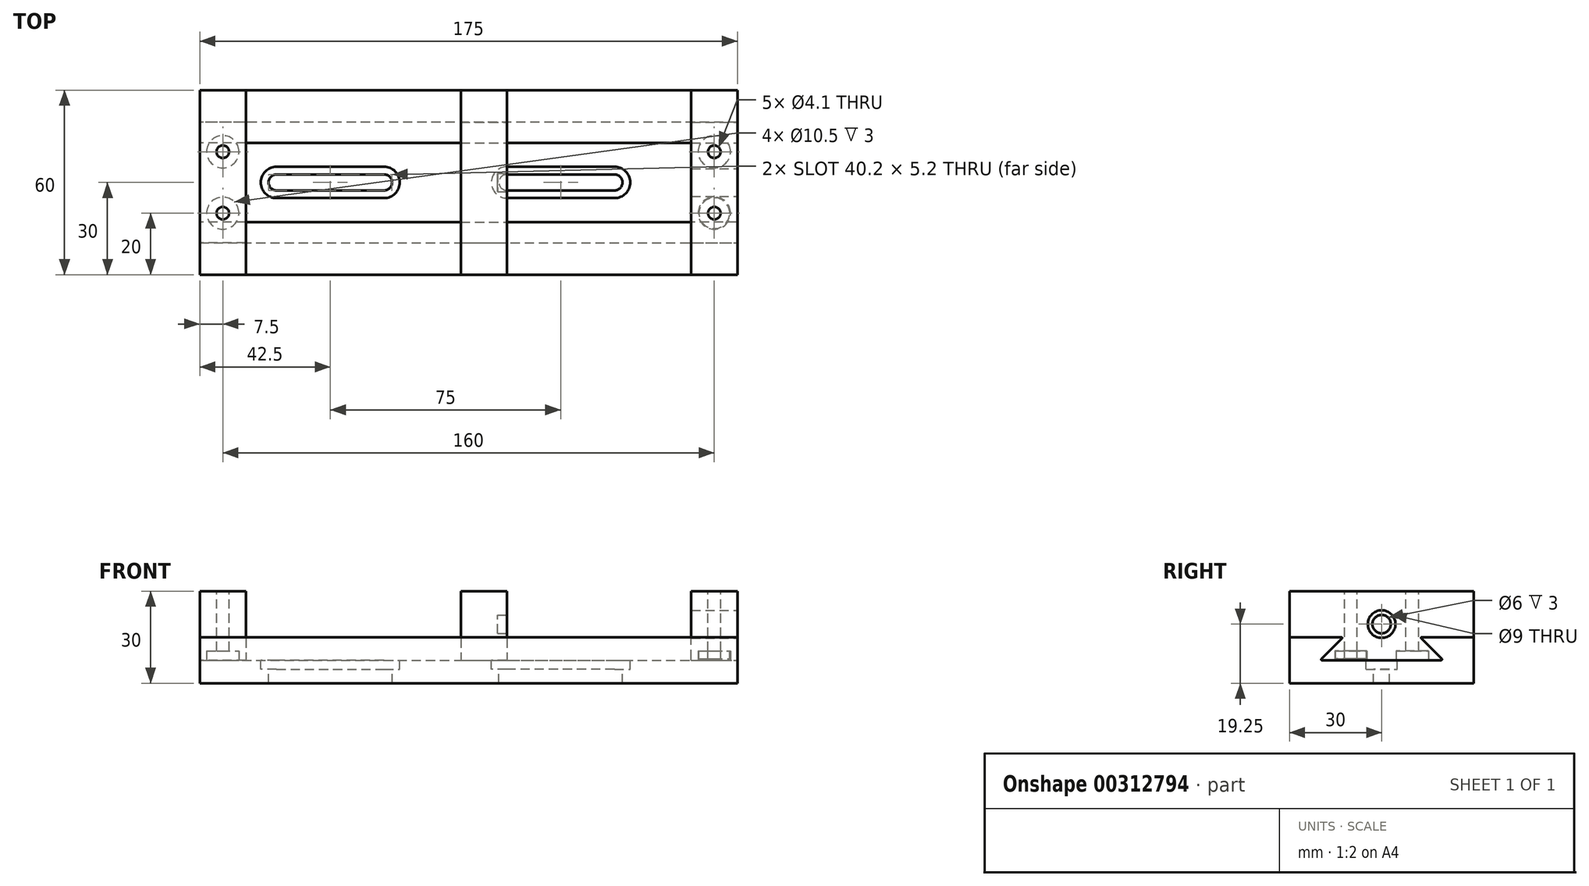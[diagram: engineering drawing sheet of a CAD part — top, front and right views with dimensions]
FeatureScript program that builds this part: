
annotation { "Feature Type Name" : "Feature", "Feature Type Description" : "" }
export const myFeature = defineFeature(function(context is Context, id is Id, definition is map)
    precondition{}
    {
        {
            var Q0;
            Q0=qCreatedBy(makeId("Top.planeOp"),FACE);
            var sketch = newSketch(context, id + "F0", { "sketchPlane" : qUnion([Q0])});
            skLineSegment(sketch, "E0.bottom", {"start": v(87.5, -30) * mm, "end": v(-87.5, -30) * mm});
            skLineSegment(sketch, "E0.top", {"start": v(87.5, 30) * mm, "end": v(-87.5, 30) * mm});
            skLineSegment(sketch, "E0.left", {"start": v(87.5, -30) * mm, "end": v(87.5, 30) * mm});
            skLineSegment(sketch, "E0.right", {"start": v(-87.5, -30) * mm, "end": v(-87.5, 30) * mm});
            skPoint(sketch, "E0.middle", {"position": v(0, 0) * mm});
            skSolve(sketch);
        }
        {
            var Q0;
            Q0=makeQuery(id+"F0.imprint","IMPRINT",FACE,{"disambiguationData":[TD([[makeQuery(id+"F0.imprint","IMPRINT",EDGE,{"derivedFrom":sQuery(id+"F0.wireOp",EDGE,"E0.bottom")}),-1.0]])]});
            extrude(context, id + "F1", {"entities" : qUnion([Q0]), "depth" : 15 * mm});
        }
        {
            var Q0;
            Q0=makeQuery(id+"F1.opExtrude","SWEPT_FACE",FACE,{"disambiguationData":[OSD([sQuery(id+"F0.wireOp",EDGE,"E0.left")])]});
            var sketch = newSketch(context, id + "F2", { "sketchPlane" : qUnion([Q0])});
            skLineSegment(sketch, "E1", {"start": v(-30, 7.5) * mm, "end": v(30, 7.5) * mm});
            skLineSegment(sketch, "E2", {"start": v(-20, 7.5) * mm, "end": v(-8.89, 18.61) * mm});
            skLineSegment(sketch, "E3", {"start": v(20, 7.5) * mm, "end": v(9.76, 17.74) * mm});
            skLineSegment(sketch, "E4", {"start": v(-8.89, 18.61) * mm, "end": v(9.76, 17.74) * mm});
            skSolve(sketch);
        }
        {
            var Q0;
            {var subQ0=sQuery(id+"F2.wireOp",EDGE,"E2");var subQ1=sQuery(id+"F2.wireOp",EDGE,"E1");var subQ2=makeQuery(id+"F2.imprint","INTERSECT",VERTEX,{"derivedFrom":[subQ1,subQ0]});Q0=makeQuery(id+"F2.imprint","IMPRINT",FACE,{"disambiguationData":[TD([[makeQuery(id+"F2.imprint","IMPRINT",EDGE,{"disambiguationData":[TD([[subQ2,-1.0]])],"derivedFrom":subQ1}),1.0]])]});}
            var Q1;
            {var subQ0=sQuery(id+"F2.wireOp",EDGE,"E4");Q1=makeQuery(id+"F2.imprint","IMPRINT",FACE,{"disambiguationData":[TD([[makeQuery(id+"F2.imprint","IMPRINT",EDGE,{"derivedFrom":subQ0}),-1.0]])]});}
            extrude(context, id + "F3", {"entities" : qUnion([Q0, Q1]), "operationType" : NewBodyOperationType.REMOVE, "endBound" : BoundingType.THROUGH_ALL, "oppositeDirection" : true, "depth" : 25 * mm});
        }
        {
            var Q0;
            Q0=makeQuery(id+"F3.boolean.opBoolean","COPY",EDGE,{"derivedFrom":makeQuery(id+"F3.opExtrude","SWEPT_EDGE",EDGE,{"disambiguationData":[OSD([sQuery(id+"F2.wireOp",EDGE,"E1"),sQuery(id+"F2.wireOp",EDGE,"E2")])]})});
            var Q1;
            Q1=makeQuery(id+"F3.boolean.opBoolean","COPY",EDGE,{"derivedFrom":makeQuery(id+"F3.opExtrude","SWEPT_EDGE",EDGE,{"disambiguationData":[OSD([sQuery(id+"F2.wireOp",EDGE,"E1"),sQuery(id+"F2.wireOp",EDGE,"E3")])]})});
            var Q2;
            Q2=makeQuery(id+"F3.boolean.opBoolean","INTERSECT",EDGE,{"derivedFrom":[makeQuery(id+"F1.opExtrude","CAP_FACE",FACE,{"disambiguationData":[OSD([sQuery(id+"F0.wireOp",EDGE,"E0.bottom"),sQuery(id+"F0.wireOp",EDGE,"E0.top"),sQuery(id+"F0.wireOp",EDGE,"E0.left"),sQuery(id+"F0.wireOp",EDGE,"E0.right")])],"isStart":false}),makeQuery(id+"F3.opExtrude","SWEPT_FACE",FACE,{"disambiguationData":[OSD([sQuery(id+"F2.wireOp",EDGE,"E3")])]})]});
            var Q3;
            Q3=makeQuery(id+"F3.boolean.opBoolean","INTERSECT",EDGE,{"derivedFrom":[makeQuery(id+"F1.opExtrude","CAP_FACE",FACE,{"disambiguationData":[OSD([sQuery(id+"F0.wireOp",EDGE,"E0.bottom"),sQuery(id+"F0.wireOp",EDGE,"E0.top"),sQuery(id+"F0.wireOp",EDGE,"E0.left"),sQuery(id+"F0.wireOp",EDGE,"E0.right")])],"isStart":false}),makeQuery(id+"F3.opExtrude","SWEPT_FACE",FACE,{"disambiguationData":[OSD([sQuery(id+"F2.wireOp",EDGE,"E2")])]})]});
            fillet(context, id + "F4", {"entities" : qUnion([Q0, Q1, Q2, Q3]), "radius" : .25 * mm, "tangentPropagation" : true, "allowEdgeOverflow" : false});
        }
        {
            var Q0;
            Q0=makeQuery(id+"F1.opExtrude","SWEPT_FACE",FACE,{"disambiguationData":[OSD([sQuery(id+"F0.wireOp",EDGE,"E0.left")])]});
            var sketch = newSketch(context, id + "F5", { "sketchPlane" : qUnion([Q0])});
            skLineSegment(sketch, "E5.0.0", {"start": v(30, 15) * mm, "end": v(13.1, 15) * mm});
            skArc(sketch, "E5.0.1", {"start": v(13.1, 15) * mm, "mid": v(12.87, 14.85) * mm, "end": v(12.93, 14.57) * mm});
            skLineSegment(sketch, "E5.0.2", {"start": v(12.93, 14.57) * mm, "end": v(19.57, 7.93) * mm});
            skArc(sketch, "E5.0.3", {"start": v(19.57, 7.93) * mm, "mid": v(19.63, 7.65) * mm, "end": v(19.4, 7.5) * mm});
            skLineSegment(sketch, "E5.0.4", {"start": v(19.4, 7.5) * mm, "end": v(-19.4, 7.5) * mm});
            skArc(sketch, "E5.0.5", {"start": v(-19.4, 7.5) * mm, "mid": v(-19.63, 7.65) * mm, "end": v(-19.57, 7.93) * mm});
            skLineSegment(sketch, "E5.0.6", {"start": v(-19.57, 7.93) * mm, "end": v(-12.93, 14.57) * mm});
            skArc(sketch, "E5.0.7", {"start": v(-12.93, 14.57) * mm, "mid": v(-12.87, 14.85) * mm, "end": v(-13.1, 15) * mm});
            skLineSegment(sketch, "E5.0.8", {"start": v(-13.1, 15) * mm, "end": v(-30, 15) * mm});
            skLineSegment(sketch, "E6.bottom", {"start": v(-30, 15) * mm, "end": v(-13.1, 15) * mm});
            skLineSegment(sketch, "E6.top", {"start": v(-30, 30) * mm, "end": v(30, 30) * mm});
            skLineSegment(sketch, "E6.left", {"start": v(-30, 15) * mm, "end": v(-30, 30) * mm});
            skLineSegment(sketch, "E6.right", {"start": v(30, 15) * mm, "end": v(30, 30) * mm});
            skLineSegment(sketch, "E7.trimOffspring", {"start": v(13.1, 15) * mm, "end": v(30, 15) * mm});
            skPoint(sketch, "E5.0.10.end.orphan", {"position": v(30, 0) * mm});
            skPoint(sketch, "E5.0.9.end.orphan", {"position": v(-30, 0) * mm});
            skSolve(sketch);
        }
        {
            var Q0;
            Q0=makeQuery(id+"F5.imprint","IMPRINT",FACE,{"disambiguationData":[TD([[makeQuery(id+"F5.imprint","IMPRINT",EDGE,{"derivedFrom":sQuery(id+"F5.wireOp",EDGE,"E5.0.1")}),-1.0]])]});
            extrude(context, id + "F6", {"entities" : qUnion([Q0]), "oppositeDirection" : true, "depth" : 15 * mm});
        }
        {
            var Q0;
            Q0=makeQuery(id+"F6.opExtrude","CAP_FACE",FACE,{"disambiguationData":[OSD([sQuery(id+"F5.wireOp",EDGE,"E5.0.1"),sQuery(id+"F5.wireOp",EDGE,"E5.0.2"),sQuery(id+"F5.wireOp",EDGE,"E5.0.3"),sQuery(id+"F5.wireOp",EDGE,"E5.0.4"),sQuery(id+"F5.wireOp",EDGE,"E5.0.5"),sQuery(id+"F5.wireOp",EDGE,"E5.0.6"),sQuery(id+"F5.wireOp",EDGE,"E5.0.7"),sQuery(id+"F5.wireOp",EDGE,"E6.bottom"),sQuery(id+"F5.wireOp",EDGE,"E6.top"),sQuery(id+"F5.wireOp",EDGE,"E6.left"),sQuery(id+"F5.wireOp",EDGE,"E6.right"),sQuery(id+"F5.wireOp",EDGE,"E7.trimOffspring")])],"isStart":true});
            var sketch = newSketch(context, id + "F7", { "sketchPlane" : qUnion([Q0])});
            skCircle(sketch, "E8", {"center": v(0, 19.25) * mm, "radius": 4.5 * mm});
            skLineSegment(sketch, "E9", {"start": v(0, 7.5) * mm, "end": v(0, 30) * mm, "construction": true});
            skSolve(sketch);
        }
        {
            var Q0;
            Q0=makeQuery(id+"F7.imprint","IMPRINT",FACE,{"disambiguationData":[TD([[makeQuery(id+"F7.imprint","IMPRINT",EDGE,{"derivedFrom":sQuery(id+"F7.wireOp",EDGE,"E8")}),1.0]])]});
            extrude(context, id + "F8", {"entities" : qUnion([Q0]), "operationType" : NewBodyOperationType.REMOVE, "endBound" : BoundingType.THROUGH_ALL, "oppositeDirection" : true, "depth" : 25 * mm});
        }
        {
            var Q0;
            Q0=makeQuery(id+"F1.opExtrude","SWEPT_FACE",FACE,{"disambiguationData":[OSD([sQuery(id+"F0.wireOp",EDGE,"E0.right")])]});
            var sketch = newSketch(context, id + "F9", { "sketchPlane" : qUnion([Q0])});
            skLineSegment(sketch, "E10.0.0", {"start": v(-19.57, 7.93) * mm, "end": v(-12.93, 14.57) * mm});
            skArc(sketch, "E10.0.1", {"start": v(-12.93, 14.57) * mm, "mid": v(-12.87, 14.85) * mm, "end": v(-13.1, 15) * mm});
            skLineSegment(sketch, "E10.0.2", {"start": v(-13.1, 15) * mm, "end": v(-30, 15) * mm});
            skLineSegment(sketch, "E10.0.6", {"start": v(30, 15) * mm, "end": v(13.1, 15) * mm});
            skArc(sketch, "E10.0.7", {"start": v(13.1, 15) * mm, "mid": v(12.87, 14.85) * mm, "end": v(12.93, 14.57) * mm});
            skLineSegment(sketch, "E10.0.8", {"start": v(12.93, 14.57) * mm, "end": v(19.57, 7.93) * mm});
            skArc(sketch, "E10.0.9", {"start": v(19.57, 7.93) * mm, "mid": v(19.63, 7.65) * mm, "end": v(19.4, 7.5) * mm});
            skLineSegment(sketch, "E10.0.10", {"start": v(19.4, 7.5) * mm, "end": v(-19.4, 7.5) * mm});
            skArc(sketch, "E10.0.11", {"start": v(-19.4, 7.5) * mm, "mid": v(-19.63, 7.65) * mm, "end": v(-19.57, 7.93) * mm});
            skLineSegment(sketch, "E11.bottom", {"start": v(-30, 15) * mm, "end": v(-13.1, 15) * mm});
            skLineSegment(sketch, "E11.top", {"start": v(-30, 30) * mm, "end": v(30, 30) * mm});
            skLineSegment(sketch, "E11.left", {"start": v(-30, 15) * mm, "end": v(-30, 30) * mm});
            skLineSegment(sketch, "E11.right", {"start": v(30, 15) * mm, "end": v(30, 30) * mm});
            skLineSegment(sketch, "E12.trimOffspring", {"start": v(13.1, 15) * mm, "end": v(30, 15) * mm});
            skPoint(sketch, "E10.0.4.end.orphan", {"position": v(30, 0) * mm});
            skPoint(sketch, "E10.0.3.end.orphan", {"position": v(-30, 0) * mm});
            skSolve(sketch);
        }
        {
            var Q0;
            Q0=makeQuery(id+"F9.imprint","IMPRINT",FACE,{"disambiguationData":[TD([[makeQuery(id+"F9.imprint","IMPRINT",EDGE,{"derivedFrom":sQuery(id+"F9.wireOp",EDGE,"E10.0.0")}),1.0]])]});
            extrude(context, id + "F10", {"entities" : qUnion([Q0]), "oppositeDirection" : true, "depth" : 15 * mm});
        }
        {
            var Q0;
            Q0=makeQuery(id+"F1.opExtrude","SWEPT_FACE",FACE,{"disambiguationData":[OSD([sQuery(id+"F0.wireOp",EDGE,"E0.right")])]});
            cPlane(context, id + "F11", {"entities" : qUnion([Q0]), "cplaneType" : CPlaneType.OFFSET, "offset" : 100 * mm, "oppositeDirection" : true, "width" : 150 * mm, "height" : 150 * mm});
        }
        {
            var Q0;
            Q0=qCreatedBy(id+"F11.planeOp",FACE);
            var sketch = newSketch(context, id + "F12", { "sketchPlane" : qUnion([Q0])});
            skLineSegment(sketch, "E13.0.0", {"start": v(-19.57, 7.93) * mm, "end": v(-12.93, 14.57) * mm});
            skArc(sketch, "E13.0.1", {"start": v(-12.93, 14.57) * mm, "mid": v(-12.87, 14.85) * mm, "end": v(-13.1, 15) * mm});
            skLineSegment(sketch, "E13.0.2", {"start": v(-13.1, 15) * mm, "end": v(-30, 15) * mm});
            skLineSegment(sketch, "E13.0.6", {"start": v(30, 15) * mm, "end": v(13.1, 15) * mm});
            skArc(sketch, "E13.0.7", {"start": v(13.1, 15) * mm, "mid": v(12.87, 14.85) * mm, "end": v(12.93, 14.57) * mm});
            skLineSegment(sketch, "E13.0.8", {"start": v(12.93, 14.57) * mm, "end": v(19.57, 7.93) * mm});
            skArc(sketch, "E13.0.9", {"start": v(19.57, 7.93) * mm, "mid": v(19.63, 7.65) * mm, "end": v(19.4, 7.5) * mm});
            skLineSegment(sketch, "E13.0.10", {"start": v(19.4, 7.5) * mm, "end": v(-19.4, 7.5) * mm});
            skArc(sketch, "E13.0.11", {"start": v(-19.4, 7.5) * mm, "mid": v(-19.63, 7.65) * mm, "end": v(-19.57, 7.93) * mm});
            skLineSegment(sketch, "E14.bottom", {"start": v(-30, 15) * mm, "end": v(-13.1, 15) * mm});
            skLineSegment(sketch, "E14.top", {"start": v(-30, 30) * mm, "end": v(30, 30) * mm});
            skLineSegment(sketch, "E14.left", {"start": v(-30, 15) * mm, "end": v(-30, 30) * mm});
            skLineSegment(sketch, "E14.right", {"start": v(30, 15) * mm, "end": v(30, 30) * mm});
            skLineSegment(sketch, "E15.trimOffspring", {"start": v(13.1, 15) * mm, "end": v(30, 15) * mm});
            skPoint(sketch, "E13.0.4.end.orphan", {"position": v(30, 0) * mm});
            skPoint(sketch, "E13.0.3.end.orphan", {"position": v(-30, 0) * mm});
            skSolve(sketch);
        }
        {
            var Q0;
            Q0=makeQuery(id+"F12.imprint","IMPRINT",FACE,{"disambiguationData":[TD([[makeQuery(id+"F12.imprint","IMPRINT",EDGE,{"derivedFrom":sQuery(id+"F12.wireOp",EDGE,"E13.0.0")}),-1.0]])]});
            extrude(context, id + "F13", {"entities" : qUnion([Q0]), "depth" : 15 * mm});
        }
        {
            var Q0;
            Q0=makeQuery(id+"F13.opExtrude","CAP_FACE",FACE,{"disambiguationData":[OSD([sQuery(id+"F12.wireOp",EDGE,"E13.0.0"),sQuery(id+"F12.wireOp",EDGE,"E13.0.1"),sQuery(id+"F12.wireOp",EDGE,"E13.0.7"),sQuery(id+"F12.wireOp",EDGE,"E13.0.8"),sQuery(id+"F12.wireOp",EDGE,"E13.0.9"),sQuery(id+"F12.wireOp",EDGE,"E13.0.10"),sQuery(id+"F12.wireOp",EDGE,"E13.0.11"),sQuery(id+"F12.wireOp",EDGE,"E14.bottom"),sQuery(id+"F12.wireOp",EDGE,"E14.top"),sQuery(id+"F12.wireOp",EDGE,"E14.left"),sQuery(id+"F12.wireOp",EDGE,"E14.right"),sQuery(id+"F12.wireOp",EDGE,"E15.trimOffspring")])],"isStart":true});
            var sketch = newSketch(context, id + "F14", { "sketchPlane" : qUnion([Q0])});
            skCircle(sketch, "E16", {"center": v(0, 19.25) * mm, "radius": 3 * mm});
            skSolve(sketch);
        }
        {
            var Q0;
            Q0=makeQuery(id+"F14.imprint","IMPRINT",FACE,{"disambiguationData":[TD([[makeQuery(id+"F14.imprint","IMPRINT",EDGE,{"derivedFrom":sQuery(id+"F14.wireOp",EDGE,"E16")}),1.0]])]});
            extrude(context, id + "F15", {"entities" : qUnion([Q0]), "operationType" : NewBodyOperationType.REMOVE, "oppositeDirection" : true, "depth" : 3 * mm});
        }
        {
            var Q0;
            Q0=makeQuery(id+"F6.opExtrude","SWEPT_FACE",FACE,{"disambiguationData":[OSD([sQuery(id+"F5.wireOp",EDGE,"E6.top")])]});
            var sketch = newSketch(context, id + "F16", { "sketchPlane" : qUnion([Q0])});
            skLineSegment(sketch, "E17", {"start": v(80, 30) * mm, "end": v(80, -30) * mm, "construction": true});
            skCircle(sketch, "E18", {"center": v(80, 10) * mm, "radius": 2.05 * mm});
            skCircle(sketch, "E19", {"center": v(80, -10) * mm, "radius": 2.05 * mm});
            skLineSegment(sketch, "E20", {"start": v(72.5, 0) * mm, "end": v(87.5, 0) * mm, "construction": true});
            skSolve(sketch);
        }
        {
            var Q0;
            Q0=makeQuery(id+"F16.imprint","IMPRINT",FACE,{"disambiguationData":[TD([[makeQuery(id+"F16.imprint","IMPRINT",EDGE,{"derivedFrom":sQuery(id+"F16.wireOp",EDGE,"E18")}),1.0]])]});
            var Q1;
            Q1=makeQuery(id+"F16.imprint","IMPRINT",FACE,{"disambiguationData":[TD([[makeQuery(id+"F16.imprint","IMPRINT",EDGE,{"derivedFrom":sQuery(id+"F16.wireOp",EDGE,"E19")}),1.0]])]});
            var Q2;
            Q2=makeQuery(id+"F3.boolean.opBoolean","COPY",FACE,{"derivedFrom":makeQuery(id+"F3.opExtrude","SWEPT_FACE",FACE,{"disambiguationData":[OSD([sQuery(id+"F2.wireOp",EDGE,"E1")])]})});
            extrude(context, id + "F17", {"entities" : qUnion([Q0, Q1]), "operationType" : NewBodyOperationType.REMOVE, "endBound" : BoundingType.UP_TO_SURFACE, "oppositeDirection" : true, "endBoundEntityFace" : qUnion([Q2]), "depth" : 25 * mm});
        }
        {
            var Q0;
            Q0=makeQuery(id+"F10.opExtrude","SWEPT_FACE",FACE,{"disambiguationData":[OSD([sQuery(id+"F9.wireOp",EDGE,"E11.top")])]});
            var sketch = newSketch(context, id + "F18", { "sketchPlane" : qUnion([Q0])});
            skLineSegment(sketch, "E21", {"start": v(-80, 30) * mm, "end": v(-80, -30) * mm, "construction": true});
            skLineSegment(sketch, "E22", {"start": v(-72.5, 0) * mm, "end": v(-87.5, 0) * mm, "construction": true});
            skCircle(sketch, "E23", {"center": v(-80, 10) * mm, "radius": 2.05 * mm});
            skCircle(sketch, "E24", {"center": v(-80, -10) * mm, "radius": 2.05 * mm});
            skSolve(sketch);
        }
        {
            var Q0;
            Q0=makeQuery(id+"F18.imprint","IMPRINT",FACE,{"disambiguationData":[TD([[makeQuery(id+"F18.imprint","IMPRINT",EDGE,{"derivedFrom":sQuery(id+"F18.wireOp",EDGE,"E23")}),1.0]])]});
            var Q1;
            Q1=makeQuery(id+"F18.imprint","IMPRINT",FACE,{"disambiguationData":[TD([[makeQuery(id+"F18.imprint","IMPRINT",EDGE,{"derivedFrom":sQuery(id+"F18.wireOp",EDGE,"E24")}),1.0]])]});
            var Q2;
            Q2=makeQuery(id+"F3.boolean.opBoolean","COPY",FACE,{"derivedFrom":makeQuery(id+"F3.opExtrude","SWEPT_FACE",FACE,{"disambiguationData":[OSD([sQuery(id+"F2.wireOp",EDGE,"E1")])]})});
            extrude(context, id + "F19", {"entities" : qUnion([Q0, Q1]), "operationType" : NewBodyOperationType.REMOVE, "endBound" : BoundingType.UP_TO_SURFACE, "oppositeDirection" : true, "endBoundEntityFace" : qUnion([Q2]), "depth" : 25 * mm});
        }
        {
            var Q0;
            Q0=makeQuery(id+"F10.opExtrude","SWEPT_FACE",FACE,{"disambiguationData":[OSD([sQuery(id+"F9.wireOp",EDGE,"E10.0.10")])]});
            var sketch = newSketch(context, id + "F20", { "sketchPlane" : qUnion([Q0])});
            skCircle(sketch, "E25", {"center": v(-80, 10) * mm, "radius": 5.25 * mm});
            skCircle(sketch, "E26", {"center": v(-80, -10) * mm, "radius": 5.25 * mm});
            skSolve(sketch);
        }
        {
            var Q0;
            Q0=makeQuery(id+"F20.imprint","IMPRINT",FACE,{"disambiguationData":[TD([[makeQuery(id+"F20.imprint","IMPRINT",EDGE,{"derivedFrom":sQuery(id+"F20.wireOp",EDGE,"E25")}),1.0]])]});
            var Q1;
            Q1=makeQuery(id+"F20.imprint","IMPRINT",FACE,{"disambiguationData":[TD([[makeQuery(id+"F20.imprint","IMPRINT",EDGE,{"derivedFrom":sQuery(id+"F20.wireOp",EDGE,"E26")}),1.0]])]});
            extrude(context, id + "F21", {"entities" : qUnion([Q0, Q1]), "operationType" : NewBodyOperationType.REMOVE, "oppositeDirection" : true, "depth" : 3 * mm});
        }
        {
            var Q0;
            Q0=makeQuery(id+"F6.opExtrude","SWEPT_FACE",FACE,{"disambiguationData":[OSD([sQuery(id+"F5.wireOp",EDGE,"E5.0.4")])]});
            var sketch = newSketch(context, id + "F22", { "sketchPlane" : qUnion([Q0])});
            skCircle(sketch, "E27", {"center": v(80, 10) * mm, "radius": 5.25 * mm});
            skCircle(sketch, "E28", {"center": v(80, -10) * mm, "radius": 5.25 * mm});
            skSolve(sketch);
        }
        {
            var Q0;
            Q0=makeQuery(id+"F22.imprint","IMPRINT",FACE,{"disambiguationData":[TD([[makeQuery(id+"F22.imprint","IMPRINT",EDGE,{"derivedFrom":sQuery(id+"F22.wireOp",EDGE,"E27")}),1.0]])]});
            var Q1;
            Q1=makeQuery(id+"F22.imprint","IMPRINT",FACE,{"disambiguationData":[TD([[makeQuery(id+"F22.imprint","IMPRINT",EDGE,{"derivedFrom":sQuery(id+"F22.wireOp",EDGE,"E28")}),1.0]])]});
            extrude(context, id + "F23", {"entities" : qUnion([Q0, Q1]), "operationType" : NewBodyOperationType.REMOVE, "oppositeDirection" : true, "depth" : 3 * mm});
        }
        {
            var Q0;
            Q0=makeQuery(id+"F23.boolean.opBoolean","COPY",FACE,{"derivedFrom":makeQuery(id+"F23.opExtrude","CAP_FACE",FACE,{"disambiguationData":[OSD([sQuery(id+"F2.wireOp",EDGE,"E1"),sQuery(id+"F16.wireOp",EDGE,"E19"),sQuery(id+"F22.wireOp",EDGE,"E27")])],"isStart":false})});
            var sketch = newSketch(context, id + "F24", { "sketchPlane" : qUnion([Q0])});
            skCircle(sketch, "E29", {"center": v(80, 10) * mm, "radius": 5 * mm});
            skSolve(sketch);
        }
        {
            var Q0;
            Q0=makeQuery(id+"F24.imprint","IMPRINT",FACE,{"disambiguationData":[TD([[makeQuery(id+"F24.imprint","IMPRINT",EDGE,{"derivedFrom":sQuery(id+"F24.wireOp",EDGE,"E29")}),1.0]])]});
            var Q1;
            Q1=makeQuery(id+"F24.imprint","IMPRINT",FACE,{"disambiguationData":[TD([[makeQuery(id+"F24.imprint","IMPRINT",EDGE,{"derivedFrom":makeQuery(id+"F23.boolean.opBoolean","COPY",EDGE,{"derivedFrom":makeQuery(id+"F23.opExtrude","CAP_EDGE",EDGE,{"disambiguationData":[OSD([sQuery(id+"F2.wireOp",EDGE,"E1"),sQuery(id+"F16.wireOp",EDGE,"E19")])],"isStart":false})})}),-1.0]])]});
            extrude(context, id + "F25", {"entities" : qUnion([Q0, Q1]), "depth" : 2.5 * mm});
        }
        {
            var Q0;
            Q0=makeQuery(id+"F3.boolean.opBoolean","COPY",FACE,{"derivedFrom":makeQuery(id+"F3.opExtrude","SWEPT_FACE",FACE,{"disambiguationData":[OSD([sQuery(id+"F2.wireOp",EDGE,"E1")])]})});
            var sketch = newSketch(context, id + "F26", { "sketchPlane" : qUnion([Q0])});
            skLineSegment(sketch, "E30", {"start": v(12.5, 0) * mm, "end": v(47.5, 0) * mm});
            skLineSegment(sketch, "E31", {"start": v(-27.5, 0) * mm, "end": v(-62.5, 0) * mm});
            skArc(sketch, "E32.0.startCap", {"start": v(-27.5, 2.6) * mm, "mid": v(-24.9, 0) * mm, "end": v(-27.5, -2.6) * mm});
            skArc(sketch, "E32.0.endCap", {"start": v(-62.5, -2.6) * mm, "mid": v(-65.1, 0) * mm, "end": v(-62.5, 2.6) * mm});
            skLineSegment(sketch, "E32.0.left", {"start": v(-27.5, -2.6) * mm, "end": v(-62.5, -2.6) * mm});
            skLineSegment(sketch, "E32.0.right", {"start": v(-27.5, 2.6) * mm, "end": v(-62.5, 2.6) * mm});
            skArc(sketch, "E32.1.startCap", {"start": v(12.5, -2.6) * mm, "mid": v(9.9, 0) * mm, "end": v(12.5, 2.6) * mm});
            skArc(sketch, "E32.1.endCap", {"start": v(47.5, 2.6) * mm, "mid": v(50.1, 0) * mm, "end": v(47.5, -2.6) * mm});
            skLineSegment(sketch, "E32.1.left", {"start": v(12.5, 2.6) * mm, "end": v(47.5, 2.6) * mm});
            skLineSegment(sketch, "E32.1.right", {"start": v(12.5, -2.6) * mm, "end": v(47.5, -2.6) * mm});
            skSolve(sketch);
        }
        {
            var Q0;
            Q0=qSketchRegion(id+"F26",true);
            extrude(context, id + "F27", {"entities" : qUnion([Q0]), "operationType" : NewBodyOperationType.REMOVE, "oppositeDirection" : true, "depth" : 25 * mm});
        }
        {
            var Q0;
            Q0=makeQuery(id+"F3.boolean.opBoolean","COPY",FACE,{"derivedFrom":makeQuery(id+"F3.opExtrude","SWEPT_FACE",FACE,{"disambiguationData":[OSD([sQuery(id+"F2.wireOp",EDGE,"E1")])]})});
            var sketch = newSketch(context, id + "F28", { "sketchPlane" : qUnion([Q0])});
            skLineSegment(sketch, "E33", {"start": v(-27.5, 0) * mm, "end": v(-62.5, 0) * mm});
            skLineSegment(sketch, "E34", {"start": v(12.5, 0) * mm, "end": v(47.5, 0) * mm});
            skArc(sketch, "E35.0.startCap", {"start": v(12.5, -5.1) * mm, "mid": v(7.4, 0) * mm, "end": v(12.5, 5.1) * mm});
            skArc(sketch, "E35.0.endCap", {"start": v(47.5, 5.1) * mm, "mid": v(52.6, 0) * mm, "end": v(47.5, -5.1) * mm});
            skLineSegment(sketch, "E35.0.left", {"start": v(12.5, 5.1) * mm, "end": v(47.5, 5.1) * mm});
            skLineSegment(sketch, "E35.0.right", {"start": v(12.5, -5.1) * mm, "end": v(47.5, -5.1) * mm});
            skArc(sketch, "E35.1.startCap", {"start": v(-27.5, 5.1) * mm, "mid": v(-22.4, 0) * mm, "end": v(-27.5, -5.1) * mm});
            skArc(sketch, "E35.1.endCap", {"start": v(-62.5, -5.1) * mm, "mid": v(-67.6, 0) * mm, "end": v(-62.5, 5.1) * mm});
            skLineSegment(sketch, "E35.1.left", {"start": v(-27.5, -5.1) * mm, "end": v(-62.5, -5.1) * mm});
            skLineSegment(sketch, "E35.1.right", {"start": v(-27.5, 5.1) * mm, "end": v(-62.5, 5.1) * mm});
            skSolve(sketch);
        }
        {
            var Q0;
            Q0=qSketchRegion(id+"F28",true);
            extrude(context, id + "F29", {"entities" : qUnion([Q0]), "operationType" : NewBodyOperationType.REMOVE, "oppositeDirection" : true, "depth" : 3 * mm});
        }
    });
